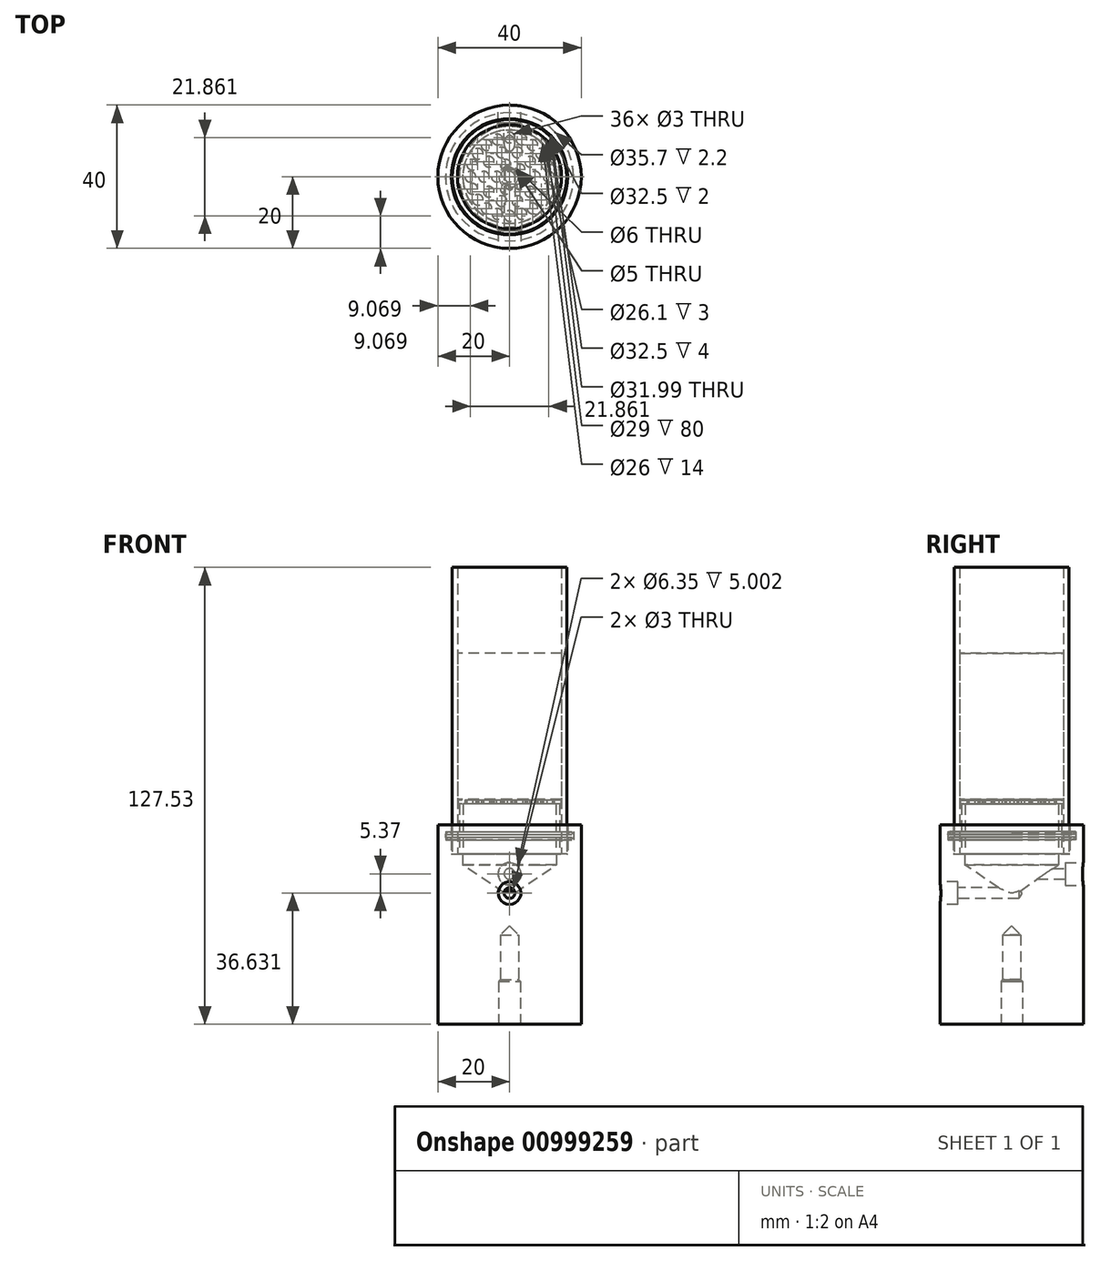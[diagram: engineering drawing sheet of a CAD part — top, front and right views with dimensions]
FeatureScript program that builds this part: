
annotation { "Feature Type Name" : "Feature", "Feature Type Description" : "" }
export const myFeature = defineFeature(function(context is Context, id is Id, definition is map)
    precondition{}
    {
        {
            var Q0;
            Q0=qCreatedBy(makeId("Top.planeOp"),FACE);
            var sketch = newSketch(context, id + "F0", { "sketchPlane" : qUnion([Q0])});
            skCircle(sketch, "E0", {"center": v(0, 0) * mm, "radius": 16 * mm});
            skCircle(sketch, "E1", {"center": v(0, 0) * mm, "radius": 14.5 * mm});
            skSolve(sketch);
        }
        {
            var Q0;
            Q0=makeQuery(id+"F0.imprint","IMPRINT",FACE,{"disambiguationData":[TD([[makeQuery(id+"F0.imprint","IMPRINT",EDGE,{"derivedFrom":sQuery(id+"F0.wireOp",EDGE,"E0")}),1.0]])]});
            extrude(context, id + "F1", {"entities" : qUnion([Q0]), "depth" : 80 * mm, "offsetDistance" : 25 * mm});
        }
        {
            var Q0;
            Q0=qCreatedBy(makeId("Front.planeOp"),FACE);
            var sketch = newSketch(context, id + "F2", { "sketchPlane" : qUnion([Q0])});
            skLineSegment(sketch, "E2", {"start": v(-16.25, 0) * mm, "end": v(-16.25, 4) * mm});
            skLineSegment(sketch, "E3", {"start": v(-16.25, 8.2) * mm, "end": v(-20, 8.1) * mm});
            skLineSegment(sketch, "E4", {"start": v(-20, 8.1) * mm, "end": v(-20, -47.53) * mm});
            skLineSegment(sketch, "E5", {"start": v(-20, -47.53) * mm, "end": v(-3, -47.53) * mm});
            skLineSegment(sketch, "E6", {"start": v(0, -20.03) * mm, "end": v(0, -11.9) * mm});
            skLineSegment(sketch, "E7", {"start": v(0, -11.9) * mm, "end": v(-13.05, -3) * mm});
            skLineSegment(sketch, "E8", {"start": v(-13.05, -3) * mm, "end": v(-13.05, 0) * mm});
            skLineSegment(sketch, "E9", {"start": v(-13.05, 0) * mm, "end": v(-16.25, 0) * mm});
            skLineSegment(sketch, "E10", {"start": v(-16.25, 6.2) * mm, "end": v(-17.85, 6.2) * mm});
            skLineSegment(sketch, "E11", {"start": v(-17.85, 6.2) * mm, "end": v(-17.85, 4) * mm});
            skLineSegment(sketch, "E12", {"start": v(-17.85, 4) * mm, "end": v(-16.25, 4) * mm});
            skLineSegment(sketch, "E13.trimOffspring", {"start": v(-16.25, 6.2) * mm, "end": v(-16.25, 8.2) * mm});
            skLineSegment(sketch, "E14", {"start": v(-3, -47.53) * mm, "end": v(-3, -35.53) * mm});
            skLineSegment(sketch, "E15", {"start": v(-2.5, -22.53) * mm, "end": v(-2.5, -35.03) * mm});
            skLineSegment(sketch, "E16", {"start": v(-3, -35.53) * mm, "end": v(-2.5, -35.03) * mm});
            skPoint(sketch, "E17.orphan", {"position": v(0, -47.53) * mm});
            skLineSegment(sketch, "E18", {"start": v(-2.5, -22.53) * mm, "end": v(0, -20.03) * mm});
            skSolve(sketch);
        }
        {
            var Q0;
            Q0=makeQuery(id+"F2.imprint","IMPRINT",FACE,{"disambiguationData":[TD([[makeQuery(id+"F2.imprint","IMPRINT",EDGE,{"derivedFrom":sQuery(id+"F2.wireOp",EDGE,"E2")}),1.0]])]});
            var Q1;
            Q1=sQuery(id+"F2.wireOp",EDGE,"E6");
            revolve(context, id + "F3", {"surfaceOperationType" : NewSurfaceOperationType.NEW, "entities" : qUnion([Q0]), "axis" : qUnion([Q1]), "revolveType" : RevolveType.FULL});
        }
        {
            var Q0;
            Q0=qCreatedBy(makeId("Front.planeOp"),FACE);
            cPlane(context, id + "F4", {"entities" : qUnion([Q0]), "cplaneType" : CPlaneType.OFFSET, "offset" : 20 * mm, "width" : 150 * mm, "height" : 150 * mm});
        }
        {
            var Q0;
            Q0=qCreatedBy(id+"F4.planeOp",FACE);
            var sketch = newSketch(context, id + "F5", { "sketchPlane" : qUnion([Q0])});
            skLineSegment(sketch, "E19", {"start": v(0, -39.9) * mm, "end": v(0, -10.9) * mm});
            skSolve(sketch);
        }
        {
            var Q0;
            Q0=qCreatedBy(makeId("Front.planeOp"),FACE);
            var Q1;
            Q1 = qBodyType(qCreatedBy(id + "F7" ,EDGE), BodyType.WIRE);
            cPlane(context, id + "F6", {"entities" : qUnion([Q0, Q1]), "cplaneType" : CPlaneType.OFFSET, "offset" : 20 * mm, "oppositeDirection" : true, "width" : 150 * mm, "height" : 150 * mm});
        }
        {
            var Q0;
            Q0=qCreatedBy(id+"F6.planeOp",FACE);
            var sketch = newSketch(context, id + "F7", { "sketchPlane" : qUnion([Q0])});
            skLineSegment(sketch, "E20", {"start": v(0, -47.53) * mm, "end": v(0, -5.53) * mm});
            skSolve(sketch);
        }
        {
            var Q0;
            Q0=sQuery(id+"F7.wireOp",VERTEX,"E20.end");
            var Q1;
            Q1=makeQuery(id+"F3.opRevolve","SWEPT_BODY",BODY,{"disambiguationData":[OSD([sQuery(id+"F2.wireOp",EDGE,"E2"),sQuery(id+"F2.wireOp",EDGE,"E3"),sQuery(id+"F2.wireOp",EDGE,"E4"),sQuery(id+"F2.wireOp",EDGE,"E5"),sQuery(id+"F2.wireOp",EDGE,"E6"),sQuery(id+"F2.wireOp",EDGE,"E7"),sQuery(id+"F2.wireOp",EDGE,"E8"),sQuery(id+"F2.wireOp",EDGE,"E9")])]});
            hole(context, id + "F8", {"style" : HoleStyle.C_BORE, "endStyle" : HoleEndStyle.BLIND, "oppositeDirection" : true, "holeDiameter" : 3 * mm, "cBoreDiameter" : 6.35 * mm, "cBoreDepth" : 5 * mm, "majorDiameter" : 5 * mm, "holeDepth" : 22 * mm, "isTappedThrough" : true, "tappedDepth" : 12 * mm, "tapClearance" : 3, "startFromSketch" : true, "locations" : qUnion([Q0]), "scope" : qUnion([Q1])});
        }
        {
            var Q0;
            Q0=makeQuery(id+"F1.opExtrude","SWEPT_BODY",BODY,{"disambiguationData":[OSD([sQuery(id+"F0.wireOp",EDGE,"E0"),sQuery(id+"F0.wireOp",EDGE,"E1")])]});
            transform(context, id + "F9", {"entities" : qUnion([Q0]), "transformType" : TransformType.TRANSLATION_3D, "dx" : 0 * mm, "dy" : 0 * mm, "dz" : 0 * mm, "makeCopy" : false});
        }
        {
            var Q0;
            Q0=qCreatedBy(makeId("Top.planeOp"),FACE);
            var sketch = newSketch(context, id + "F10", { "sketchPlane" : qUnion([Q0])});
            skCircle(sketch, "E21", {"center": v(0, 0) * mm, "radius": 14.4 * mm});
            skSolve(sketch);
        }
        {
            var Q0;
            Q0=makeQuery(id+"F10.imprint","IMPRINT",FACE,{"disambiguationData":[TD([[makeQuery(id+"F10.imprint","IMPRINT",EDGE,{"derivedFrom":sQuery(id+"F10.wireOp",EDGE,"E21")}),1.0]])]});
            extrude(context, id + "F11", {"entities" : qUnion([Q0]), "depth" : 1 * mm, "offsetDistance" : 25 * mm});
        }
        {
            var Q0;
            Q0=qCreatedBy(makeId("Top.planeOp"),FACE);
            var sketch = newSketch(context, id + "F12", { "sketchPlane" : qUnion([Q0])});
            skCircle(sketch, "E22", {"center": v(0, 0) * mm, "radius": 1.5 * mm});
            skCircle(sketch, "E23", {"center": v(-3.54, 0) * mm, "radius": 1.5 * mm});
            skCircle(sketch, "E24.1.0", {"center": v(-1.1, -3.36) * mm, "radius": 1.5 * mm});
            skCircle(sketch, "E24.2.0", {"center": v(2.86, -2.08) * mm, "radius": 1.5 * mm});
            skCircle(sketch, "E24.3.0", {"center": v(2.86, 2.08) * mm, "radius": 1.5 * mm});
            skCircle(sketch, "E24.4.0", {"center": v(-1.1, 3.36) * mm, "radius": 1.5 * mm});
            skCircle(sketch, "E25", {"center": v(-7.13, 0) * mm, "radius": 1.5 * mm});
            skCircle(sketch, "E26.1.0", {"center": v(-5.77, -4.19) * mm, "radius": 1.5 * mm});
            skCircle(sketch, "E26.2.0", {"center": v(-2.2, -6.78) * mm, "radius": 1.5 * mm});
            skCircle(sketch, "E26.3.0", {"center": v(2.2, -6.78) * mm, "radius": 1.5 * mm});
            skCircle(sketch, "E26.4.0", {"center": v(5.77, -4.19) * mm, "radius": 1.5 * mm});
            skCircle(sketch, "E26.5.0", {"center": v(7.13, 0) * mm, "radius": 1.5 * mm});
            skCircle(sketch, "E26.6.0", {"center": v(5.77, 4.19) * mm, "radius": 1.5 * mm});
            skCircle(sketch, "E26.7.0", {"center": v(2.2, 6.78) * mm, "radius": 1.5 * mm});
            skCircle(sketch, "E26.8.0", {"center": v(-2.2, 6.78) * mm, "radius": 1.5 * mm});
            skCircle(sketch, "E26.9.0", {"center": v(-5.77, 4.19) * mm, "radius": 1.5 * mm});
            skCircle(sketch, "E27", {"center": v(-10.93, 0) * mm, "radius": 1.5 * mm});
            skCircle(sketch, "E28.1.0", {"center": v(-10.4, -3.38) * mm, "radius": 1.5 * mm});
            skCircle(sketch, "E28.2.0", {"center": v(-8.84, -6.42) * mm, "radius": 1.5 * mm});
            skCircle(sketch, "E28.3.0", {"center": v(-6.42, -8.84) * mm, "radius": 1.5 * mm});
            skCircle(sketch, "E28.4.0", {"center": v(-3.38, -10.4) * mm, "radius": 1.5 * mm});
            skCircle(sketch, "E28.5.0", {"center": v(0, -10.93) * mm, "radius": 1.5 * mm});
            skCircle(sketch, "E28.6.0", {"center": v(3.38, -10.4) * mm, "radius": 1.5 * mm});
            skCircle(sketch, "E28.7.0", {"center": v(6.42, -8.84) * mm, "radius": 1.5 * mm});
            skCircle(sketch, "E28.8.0", {"center": v(8.84, -6.42) * mm, "radius": 1.5 * mm});
            skCircle(sketch, "E28.9.0", {"center": v(10.4, -3.38) * mm, "radius": 1.5 * mm});
            skCircle(sketch, "E28.10.0", {"center": v(10.93, 0) * mm, "radius": 1.5 * mm});
            skCircle(sketch, "E28.11.0", {"center": v(10.4, 3.38) * mm, "radius": 1.5 * mm});
            skCircle(sketch, "E28.12.0", {"center": v(8.84, 6.42) * mm, "radius": 1.5 * mm});
            skCircle(sketch, "E28.13.0", {"center": v(6.42, 8.84) * mm, "radius": 1.5 * mm});
            skCircle(sketch, "E28.14.0", {"center": v(3.38, 10.4) * mm, "radius": 1.5 * mm});
            skCircle(sketch, "E28.15.0", {"center": v(0, 10.93) * mm, "radius": 1.5 * mm});
            skCircle(sketch, "E28.16.0", {"center": v(-3.38, 10.4) * mm, "radius": 1.5 * mm});
            skCircle(sketch, "E28.17.0", {"center": v(-6.42, 8.84) * mm, "radius": 1.5 * mm});
            skCircle(sketch, "E28.18.0", {"center": v(-8.84, 6.42) * mm, "radius": 1.5 * mm});
            skCircle(sketch, "E28.19.0", {"center": v(-10.4, 3.38) * mm, "radius": 1.5 * mm});
            skSolve(sketch);
        }
        {
            var Q0;
            Q0=makeQuery(id+"F12.imprint","IMPRINT",FACE,{"disambiguationData":[TD([[makeQuery(id+"F12.imprint","IMPRINT",EDGE,{"derivedFrom":sQuery(id+"F12.wireOp",EDGE,"E28.7.0")}),1.0]])]});
            var Q1;
            Q1=makeQuery(id+"F12.imprint","IMPRINT",FACE,{"disambiguationData":[TD([[makeQuery(id+"F12.imprint","IMPRINT",EDGE,{"derivedFrom":sQuery(id+"F12.wireOp",EDGE,"E28.3.0")}),1.0]])]});
            var Q2;
            Q2=makeQuery(id+"F12.imprint","IMPRINT",FACE,{"disambiguationData":[TD([[makeQuery(id+"F12.imprint","IMPRINT",EDGE,{"derivedFrom":sQuery(id+"F12.wireOp",EDGE,"E28.1.0")}),1.0]])]});
            var Q3;
            Q3=makeQuery(id+"F12.imprint","IMPRINT",FACE,{"disambiguationData":[TD([[makeQuery(id+"F12.imprint","IMPRINT",EDGE,{"derivedFrom":sQuery(id+"F12.wireOp",EDGE,"E28.5.0")}),1.0]])]});
            var Q4;
            Q4=makeQuery(id+"F12.imprint","IMPRINT",FACE,{"disambiguationData":[TD([[makeQuery(id+"F12.imprint","IMPRINT",EDGE,{"derivedFrom":sQuery(id+"F12.wireOp",EDGE,"E28.17.0")}),1.0]])]});
            var Q5;
            Q5=makeQuery(id+"F12.imprint","IMPRINT",FACE,{"disambiguationData":[TD([[makeQuery(id+"F12.imprint","IMPRINT",EDGE,{"derivedFrom":sQuery(id+"F12.wireOp",EDGE,"E28.14.0")}),1.0]])]});
            var Q6;
            Q6=makeQuery(id+"F12.imprint","IMPRINT",FACE,{"disambiguationData":[TD([[makeQuery(id+"F12.imprint","IMPRINT",EDGE,{"derivedFrom":sQuery(id+"F12.wireOp",EDGE,"E28.19.0")}),1.0]])]});
            var Q7;
            Q7=makeQuery(id+"F12.imprint","IMPRINT",FACE,{"disambiguationData":[TD([[makeQuery(id+"F12.imprint","IMPRINT",EDGE,{"derivedFrom":sQuery(id+"F12.wireOp",EDGE,"E28.15.0")}),1.0]])]});
            var Q8;
            Q8=makeQuery(id+"F12.imprint","IMPRINT",FACE,{"disambiguationData":[TD([[makeQuery(id+"F12.imprint","IMPRINT",EDGE,{"derivedFrom":sQuery(id+"F12.wireOp",EDGE,"E26.9.0")}),1.0]])]});
            var Q9;
            Q9=makeQuery(id+"F12.imprint","IMPRINT",FACE,{"disambiguationData":[TD([[makeQuery(id+"F12.imprint","IMPRINT",EDGE,{"derivedFrom":sQuery(id+"F12.wireOp",EDGE,"E24.3.0")}),1.0]])]});
            var Q10;
            Q10=makeQuery(id+"F12.imprint","IMPRINT",FACE,{"disambiguationData":[TD([[makeQuery(id+"F12.imprint","IMPRINT",EDGE,{"derivedFrom":sQuery(id+"F12.wireOp",EDGE,"E26.1.0")}),1.0]])]});
            var Q11;
            Q11=makeQuery(id+"F12.imprint","IMPRINT",FACE,{"disambiguationData":[TD([[makeQuery(id+"F12.imprint","IMPRINT",EDGE,{"derivedFrom":sQuery(id+"F12.wireOp",EDGE,"E28.16.0")}),1.0]])]});
            var Q12;
            Q12=makeQuery(id+"F12.imprint","IMPRINT",FACE,{"disambiguationData":[TD([[makeQuery(id+"F12.imprint","IMPRINT",EDGE,{"derivedFrom":sQuery(id+"F12.wireOp",EDGE,"E28.8.0")}),1.0]])]});
            var Q13;
            Q13=makeQuery(id+"F12.imprint","IMPRINT",FACE,{"disambiguationData":[TD([[makeQuery(id+"F12.imprint","IMPRINT",EDGE,{"derivedFrom":sQuery(id+"F12.wireOp",EDGE,"E23")}),1.0]])]});
            var Q14;
            Q14=makeQuery(id+"F12.imprint","IMPRINT",FACE,{"disambiguationData":[TD([[makeQuery(id+"F12.imprint","IMPRINT",EDGE,{"derivedFrom":sQuery(id+"F12.wireOp",EDGE,"E26.2.0")}),1.0]])]});
            var Q15;
            Q15=makeQuery(id+"F12.imprint","IMPRINT",FACE,{"disambiguationData":[TD([[makeQuery(id+"F12.imprint","IMPRINT",EDGE,{"derivedFrom":sQuery(id+"F12.wireOp",EDGE,"E26.8.0")}),1.0]])]});
            var Q16;
            Q16=makeQuery(id+"F12.imprint","IMPRINT",FACE,{"disambiguationData":[TD([[makeQuery(id+"F12.imprint","IMPRINT",EDGE,{"derivedFrom":sQuery(id+"F12.wireOp",EDGE,"E28.12.0")}),1.0]])]});
            var Q17;
            Q17=makeQuery(id+"F12.imprint","IMPRINT",FACE,{"disambiguationData":[TD([[makeQuery(id+"F12.imprint","IMPRINT",EDGE,{"derivedFrom":sQuery(id+"F12.wireOp",EDGE,"E26.7.0")}),1.0]])]});
            var Q18;
            Q18=makeQuery(id+"F12.imprint","IMPRINT",FACE,{"disambiguationData":[TD([[makeQuery(id+"F12.imprint","IMPRINT",EDGE,{"derivedFrom":sQuery(id+"F12.wireOp",EDGE,"E28.13.0")}),1.0]])]});
            var Q19;
            Q19=makeQuery(id+"F12.imprint","IMPRINT",FACE,{"disambiguationData":[TD([[makeQuery(id+"F12.imprint","IMPRINT",EDGE,{"derivedFrom":sQuery(id+"F12.wireOp",EDGE,"E22")}),1.0]])]});
            var Q20;
            Q20=makeQuery(id+"F12.imprint","IMPRINT",FACE,{"disambiguationData":[TD([[makeQuery(id+"F12.imprint","IMPRINT",EDGE,{"derivedFrom":sQuery(id+"F12.wireOp",EDGE,"E28.9.0")}),1.0]])]});
            var Q21;
            Q21=makeQuery(id+"F12.imprint","IMPRINT",FACE,{"disambiguationData":[TD([[makeQuery(id+"F12.imprint","IMPRINT",EDGE,{"derivedFrom":sQuery(id+"F12.wireOp",EDGE,"E28.10.0")}),1.0]])]});
            var Q22;
            Q22=makeQuery(id+"F12.imprint","IMPRINT",FACE,{"disambiguationData":[TD([[makeQuery(id+"F12.imprint","IMPRINT",EDGE,{"derivedFrom":sQuery(id+"F12.wireOp",EDGE,"E26.6.0")}),1.0]])]});
            var Q23;
            Q23=makeQuery(id+"F12.imprint","IMPRINT",FACE,{"disambiguationData":[TD([[makeQuery(id+"F12.imprint","IMPRINT",EDGE,{"derivedFrom":sQuery(id+"F12.wireOp",EDGE,"E26.4.0")}),1.0]])]});
            var Q24;
            Q24=makeQuery(id+"F12.imprint","IMPRINT",FACE,{"disambiguationData":[TD([[makeQuery(id+"F12.imprint","IMPRINT",EDGE,{"derivedFrom":sQuery(id+"F12.wireOp",EDGE,"E28.11.0")}),1.0]])]});
            var Q25;
            Q25=makeQuery(id+"F12.imprint","IMPRINT",FACE,{"disambiguationData":[TD([[makeQuery(id+"F12.imprint","IMPRINT",EDGE,{"derivedFrom":sQuery(id+"F12.wireOp",EDGE,"E26.3.0")}),1.0]])]});
            var Q26;
            Q26=makeQuery(id+"F12.imprint","IMPRINT",FACE,{"disambiguationData":[TD([[makeQuery(id+"F12.imprint","IMPRINT",EDGE,{"derivedFrom":sQuery(id+"F12.wireOp",EDGE,"E25")}),1.0]])]});
            var Q27;
            Q27=makeQuery(id+"F12.imprint","IMPRINT",FACE,{"disambiguationData":[TD([[makeQuery(id+"F12.imprint","IMPRINT",EDGE,{"derivedFrom":sQuery(id+"F12.wireOp",EDGE,"E24.1.0")}),1.0]])]});
            var Q28;
            Q28=makeQuery(id+"F12.imprint","IMPRINT",FACE,{"disambiguationData":[TD([[makeQuery(id+"F12.imprint","IMPRINT",EDGE,{"derivedFrom":sQuery(id+"F12.wireOp",EDGE,"E28.6.0")}),1.0]])]});
            var Q29;
            Q29=makeQuery(id+"F12.imprint","IMPRINT",FACE,{"disambiguationData":[TD([[makeQuery(id+"F12.imprint","IMPRINT",EDGE,{"derivedFrom":sQuery(id+"F12.wireOp",EDGE,"E24.2.0")}),1.0]])]});
            var Q30;
            Q30=makeQuery(id+"F12.imprint","IMPRINT",FACE,{"disambiguationData":[TD([[makeQuery(id+"F12.imprint","IMPRINT",EDGE,{"derivedFrom":sQuery(id+"F12.wireOp",EDGE,"E24.4.0")}),1.0]])]});
            var Q31;
            Q31=makeQuery(id+"F12.imprint","IMPRINT",FACE,{"disambiguationData":[TD([[makeQuery(id+"F12.imprint","IMPRINT",EDGE,{"derivedFrom":sQuery(id+"F12.wireOp",EDGE,"E28.4.0")}),1.0]])]});
            var Q32;
            Q32=makeQuery(id+"F12.imprint","IMPRINT",FACE,{"disambiguationData":[TD([[makeQuery(id+"F12.imprint","IMPRINT",EDGE,{"derivedFrom":sQuery(id+"F12.wireOp",EDGE,"E28.2.0")}),1.0]])]});
            var Q33;
            Q33=makeQuery(id+"F12.imprint","IMPRINT",FACE,{"disambiguationData":[TD([[makeQuery(id+"F12.imprint","IMPRINT",EDGE,{"derivedFrom":sQuery(id+"F12.wireOp",EDGE,"E27")}),1.0]])]});
            var Q34;
            Q34=makeQuery(id+"F12.imprint","IMPRINT",FACE,{"disambiguationData":[TD([[makeQuery(id+"F12.imprint","IMPRINT",EDGE,{"derivedFrom":sQuery(id+"F12.wireOp",EDGE,"E28.18.0")}),1.0]])]});
            var Q35;
            Q35=makeQuery(id+"F12.imprint","IMPRINT",FACE,{"disambiguationData":[TD([[makeQuery(id+"F12.imprint","IMPRINT",EDGE,{"derivedFrom":sQuery(id+"F12.wireOp",EDGE,"E26.5.0")}),1.0]])]});
            extrude(context, id + "F13", {"entities" : qUnion([Q0, Q1, Q2, Q3, Q4, Q5, Q6, Q7, Q8, Q9, Q10, Q11, Q12, Q13, Q14, Q15, Q16, Q17, Q18, Q19, Q20, Q21, Q22, Q23, Q24, Q25, Q26, Q27, Q28, Q29, Q30, Q31, Q32, Q33, Q34, Q35]), "operationType" : NewBodyOperationType.REMOVE, "depth" : 1 * mm, "offsetDistance" : 25 * mm});
        }
        {
            var Q0;
            Q0=qCreatedBy(makeId("Top.planeOp"),FACE);
            var sketch = newSketch(context, id + "F14", { "sketchPlane" : qUnion([Q0])});
            skCircle(sketch, "E29", {"center": v(0, 0) * mm, "radius": 14.5 * mm});
            skSolve(sketch);
        }
        {
            var Q0;
            Q0=makeQuery(id+"F14.imprint","IMPRINT",FACE,{"disambiguationData":[TD([[makeQuery(id+"F14.imprint","IMPRINT",EDGE,{"derivedFrom":sQuery(id+"F14.wireOp",EDGE,"E29")}),1.0]])]});
            extrude(context, id + "F15", {"entities" : qUnion([Q0]), "depth" : 40.75 * mm, "offsetDistance" : 25 * mm});
        }
        {
            var Q0;
            Q0=makeQuery(id+"F15.opExtrude","SWEPT_BODY",BODY,{"disambiguationData":[OSD([sQuery(id+"F14.wireOp",EDGE,"E29")])]});
            transform(context, id + "F16", {"entities" : qUnion([Q0]), "transformType" : TransformType.TRANSLATION_3D, "dx" : 0 * mm, "dy" : 0 * mm, "dz" : 15.25 * mm, "makeCopy" : false});
        }
        {
            var Q0;
            Q0=qCreatedBy(makeId("Front.planeOp"),FACE);
            var sketch = newSketch(context, id + "F17", { "sketchPlane" : qUnion([Q0])});
            skArc(sketch, "E30", {"start": v(-17.86, 4.74) * mm, "mid": v(-16.93, 4.1) * mm, "end": v(-16, 4.72) * mm});
            skArc(sketch, "E31.trimOffspring", {"start": v(-16, 5.47) * mm, "mid": v(-16.93, 6.1) * mm, "end": v(-17.86, 5.46) * mm});
            skLineSegment(sketch, "E32", {"start": v(-17.86, 5.46) * mm, "end": v(-17.86, 4.74) * mm});
            skLineSegment(sketch, "E33", {"start": v(-16, 5.47) * mm, "end": v(-16, 4.72) * mm});
            skSolve(sketch);
        }
        {
            var Q0;
            Q0=makeQuery(id+"F17.imprint","IMPRINT",FACE,{"disambiguationData":[TD([[makeQuery(id+"F17.imprint","IMPRINT",EDGE,{"derivedFrom":sQuery(id+"F17.wireOp",EDGE,"E30")}),1.0]])]});
            var Q1;
            Q1=sQuery(id+"F2.wireOp",EDGE,"E6");
            revolve(context, id + "F18", {"surfaceOperationType" : NewSurfaceOperationType.NEW, "entities" : qUnion([Q0]), "axis" : qUnion([Q1]), "revolveType" : RevolveType.FULL});
        }
        {
            var Q0;
            Q0=makeQuery(id+"F11.opExtrude","SWEPT_BODY",BODY,{"disambiguationData":[OSD([sQuery(id+"F10.wireOp",EDGE,"E21")])]});
            transform(context, id + "F19", {"entities" : qUnion([Q0]), "transformType" : TransformType.TRANSLATION_3D, "dx" : 0 * mm, "dy" : 0 * mm, "dz" : 14 * mm, "makeCopy" : false});
        }
        {
            var Q0;
            Q0=makeQuery(id+"F10.imprint","IMPRINT",FACE,{"disambiguationData":[TD([[makeQuery(id+"F10.imprint","IMPRINT",EDGE,{"derivedFrom":sQuery(id+"F10.wireOp",EDGE,"E21")}),1.0]])]});
            var Q1;
            Q1=sQuery(id+"F10.wireOp",EDGE,"E21");
            extrude(context, id + "F20", {"entities" : qUnion([Q0]), "surfaceEntities" : qUnion([Q1]), "depth" : 0.25 * mm, "offsetDistance" : 25 * mm});
        }
        {
            var Q0;
            Q0=makeQuery(id+"F20.opExtrude","SWEPT_BODY",BODY,{"disambiguationData":[OSD([sQuery(id+"F10.wireOp",EDGE,"E21")])]});
            transform(context, id + "F21", {"entities" : qUnion([Q0]), "transformType" : TransformType.TRANSLATION_3D, "dx" : 0 * mm, "dy" : 0 * mm, "dz" : 15 * mm, "makeCopy" : false});
        }
        {
            var Q0;
            Q0=qCreatedBy(makeId("Top.planeOp"),FACE);
            var sketch = newSketch(context, id + "F22", { "sketchPlane" : qUnion([Q0])});
            skCircle(sketch, "E34", {"center": v(0, 0) * mm, "radius": 14 * mm});
            skCircle(sketch, "E35", {"center": v(0, 0) * mm, "radius": 13 * mm});
            skSolve(sketch);
        }
        {
            var Q0;
            Q0 = qSketchRegion(id + "F22", true);
            extrude(context, id + "F23", {"entities" : qUnion([Q0]), "depth" : 14 * mm, "offsetDistance" : 25 * mm});
        }
        {
            var Q0;
            Q0=sQuery(id+"F5.wireOp",VERTEX,"E19.end");
            var Q1;
            Q1=makeQuery(id+"F3.opRevolve","SWEPT_BODY",BODY,{"disambiguationData":[OSD([sQuery(id+"F2.wireOp",EDGE,"E2"),sQuery(id+"F2.wireOp",EDGE,"E3"),sQuery(id+"F2.wireOp",EDGE,"E4"),sQuery(id+"F2.wireOp",EDGE,"E5"),sQuery(id+"F2.wireOp",EDGE,"E6"),sQuery(id+"F2.wireOp",EDGE,"E7"),sQuery(id+"F2.wireOp",EDGE,"E8"),sQuery(id+"F2.wireOp",EDGE,"E9"),sQuery(id+"F2.wireOp",EDGE,"E10"),sQuery(id+"F2.wireOp",EDGE,"E11"),sQuery(id+"F2.wireOp",EDGE,"E12"),sQuery(id+"F2.wireOp",EDGE,"E13.trimOffspring")])]});
            hole(context, id + "F24", {"style" : HoleStyle.C_BORE, "endStyle" : HoleEndStyle.BLIND, "holeDiameter" : 3 * mm, "cBoreDiameter" : 6.35 * mm, "cBoreDepth" : 5 * mm, "majorDiameter" : 5 * mm, "holeDepth" : 22 * mm, "isTappedThrough" : true, "tappedDepth" : 12 * mm, "tapClearance" : 3, "startFromSketch" : true, "locations" : qUnion([Q0]), "scope" : qUnion([Q1])});
        }
    });
